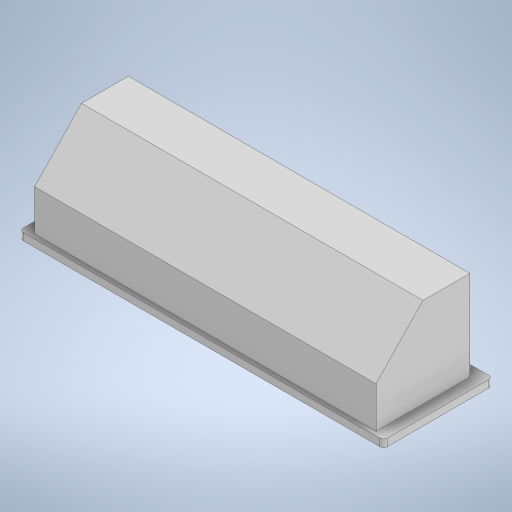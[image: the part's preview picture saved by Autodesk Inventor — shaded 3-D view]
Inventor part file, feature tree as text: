
AUTODESK INVENTOR PART (.ipt)
format: ipt  version: 2024.2 (Build 282272000, 272)  size: 232,960 bytes
history: native  units: in
note: dims shown in document units (in); Inventor stores cm internally (conversion verified against a paired STEP export)
features: extrude x3, sketch x3, fillet x1
ambient origin geometry x8: Origin, YZ Plane, XZ Plane, XY Plane, X Axis, Y Axis, Z Axis, Center Point
bodies: Solid1 (feature_tree)
feature tree (7):
  extrude  "Extrusion1"  Depth=2.0472in
  extrude  "Extrusion2"  TaperAngle=0.0deg  [1 undecoded]
  extrude  "Extrusion3"  Depth=0.1575in TaperAngle=0.0deg
  fillet  "Fillet1"  Radius=0.0787in
  sketch  "Sketch1"  dims[d0=7.1654in d1=2.0472in]
  sketch  "Sketch2"  dims[d2=1.9685in d3=0.0in d4=0.0in d5=0.0in]
  sketch  "Sketch3"  dims[d6=0.2362in d8=0.1575in d9=0.0in d10=0.0787in d7=0.0344in]
note: 1 required parameter value undecoded (feature->parameter linkage not recoverable at this tier; creation-order binding heuristic only, values carry confidence <= 0.55)
